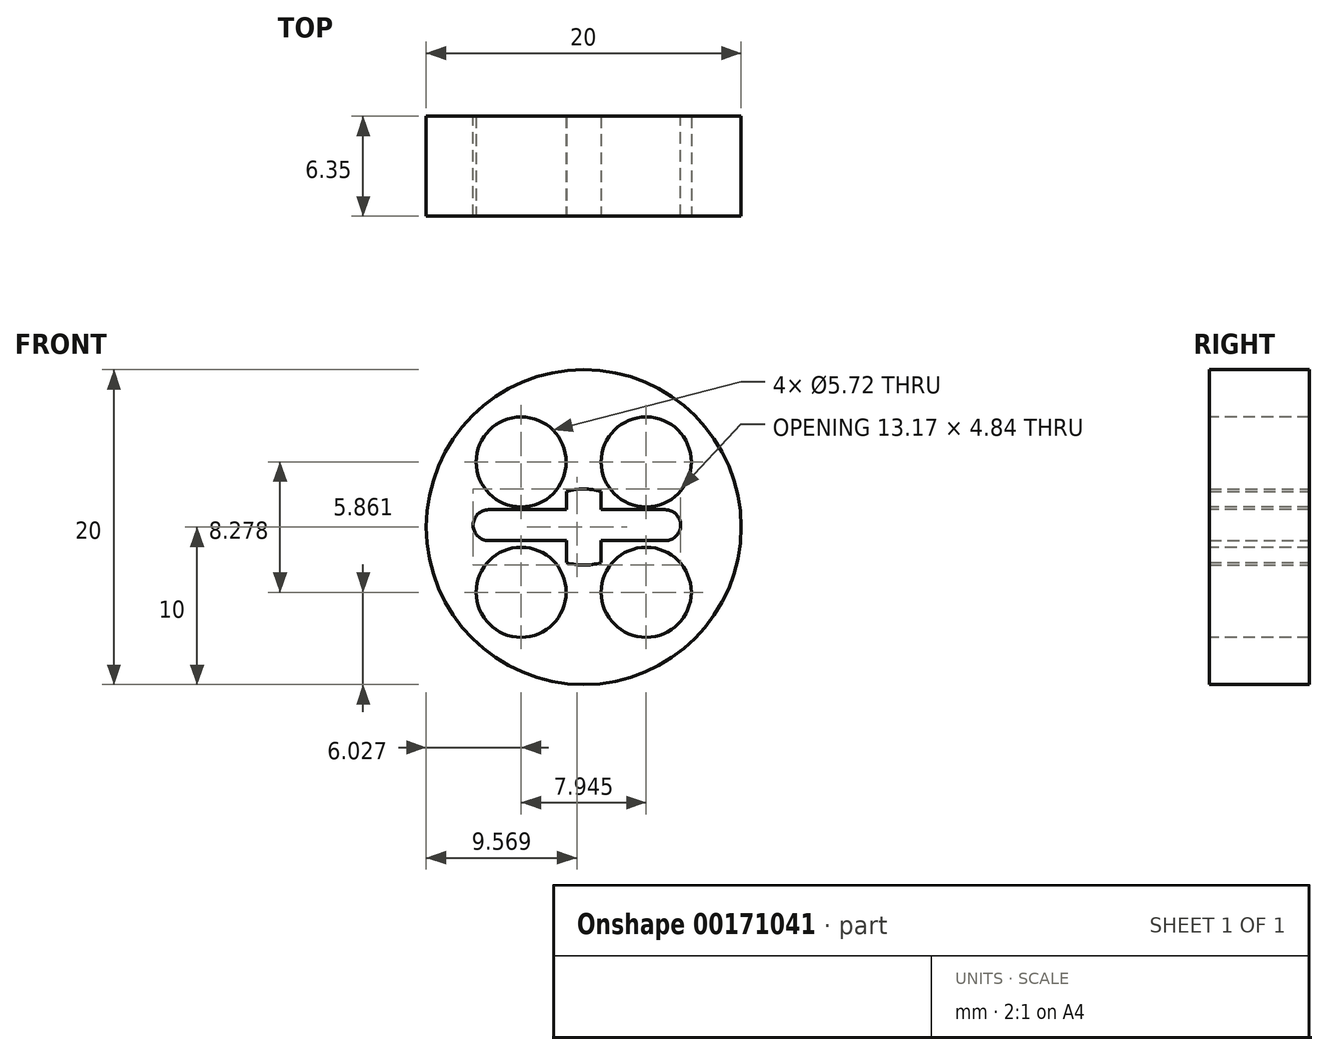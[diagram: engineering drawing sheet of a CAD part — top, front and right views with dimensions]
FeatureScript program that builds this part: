
annotation { "Feature Type Name" : "Feature", "Feature Type Description" : "" }
export const myFeature = defineFeature(function(context is Context, id is Id, definition is map)
    precondition{}
    {
        {
            var Q0;
            Q0=qCreatedBy(makeId("Front.planeOp"),FACE);
            var sketch = newSketch(context, id + "F0", { "sketchPlane" : qUnion([Q0])});
            skCircle(sketch, "E0", {"center": v(0, 0) * mm, "radius": 10 * mm});
            skSolve(sketch);
        }
        {
            var Q0;
            Q0 = qSketchRegion(id + "F0", true);
            extrude(context, id + "F1", {"entities" : qUnion([Q0]), "depth" : 6.35 * mm});
        }
        {
            var Q0;
            Q0=qCreatedBy(makeId("Front.planeOp"),FACE);
            var sketch = newSketch(context, id + "F2", { "sketchPlane" : qUnion([Q0])});
            skLineSegment(sketch, "E1", {"start": v(-6.04, 1.1) * mm, "end": v(5.17, 1.1) * mm});
            skLineSegment(sketch, "E2", {"start": v(5.17, -0.86) * mm, "end": v(-6.04, -0.86) * mm});
            skArc(sketch, "E3", {"start": v(-6.04, 1.1) * mm, "mid": v(-7.02, 0.12) * mm, "end": v(-6.04, -0.86) * mm});
            skArc(sketch, "E4", {"start": v(5.17, -0.86) * mm, "mid": v(6.16, 0.12) * mm, "end": v(5.17, 1.1) * mm});
            skSolve(sketch);
        }
        {
            var Q0;
            Q0 = qSketchRegion(id + "F2", true);
            extrude(context, id + "F3", {"entities" : qUnion([Q0]), "operationType" : NewBodyOperationType.REMOVE, "depth" : 25.4 * mm});
        }
        {
            var Q0;
            Q0=qCreatedBy(makeId("Front.planeOp"),FACE);
            var sketch = newSketch(context, id + "F4", { "sketchPlane" : qUnion([Q0])});
            skLineSegment(sketch, "E5", {"start": v(1.1, 0) * mm, "end": v(1.1, 2.26) * mm});
            skLineSegment(sketch, "E6", {"start": v(-1.1, 0) * mm, "end": v(-1.1, 2.26) * mm});
            skArc(sketch, "E7", {"start": v(1.1, 2.26) * mm, "mid": v(0, 2.42) * mm, "end": v(-1.1, 2.26) * mm});
            skLineSegment(sketch, "E8.MirrorCS", {"start": v(-1.1, 0) * mm, "end": v(-1.1, -2.26) * mm});
            skLineSegment(sketch, "E9.MirrorCS", {"start": v(1.1, 0) * mm, "end": v(1.1, -2.26) * mm});
            skArc(sketch, "E10.MirrorCS", {"start": v(1.1, -2.26) * mm, "mid": v(0, -2.42) * mm, "end": v(-1.1, -2.26) * mm});
            skSolve(sketch);
        }
        {
            var Q0;
            Q0 = qSketchRegion(id + "F4", true);
            extrude(context, id + "F5", {"entities" : qUnion([Q0]), "operationType" : NewBodyOperationType.REMOVE, "depth" : 25.4 * mm});
        }
        {
            var Q0;
            Q0=makeQuery(id+"F1.opExtrude","CAP_FACE",FACE,{"disambiguationData":[OSD([sQuery(id+"F0.wireOp",EDGE,"E0")])],"isStart":false});
            var sketch = newSketch(context, id + "F6", { "sketchPlane" : qUnion([Q0])});
            skCircle(sketch, "E11", {"center": v(-3.97, 4.14) * mm, "radius": 2.86 * mm});
            skPoint(sketch, "E12.centerSnap0", {"position": v(-3.57, -0.86) * mm});
            skLineSegment(sketch, "E13", {"start": v(0, 0) * mm, "end": v(-9.75, 0) * mm});
            skCircle(sketch, "E14.MirrorC", {"center": v(-3.97, -4.14) * mm, "radius": 2.86 * mm});
            skPoint(sketch, "E15.endSnap0", {"position": v(0, 2.42) * mm});
            skCircle(sketch, "E16.MirrorC", {"center": v(3.97, 4.14) * mm, "radius": 2.86 * mm});
            skCircle(sketch, "E17.MirrorC", {"center": v(3.97, -4.14) * mm, "radius": 2.86 * mm});
            skSolve(sketch);
        }
        {
            var Q0;
            Q0 = qSketchRegion(id + "F6", true);
            extrude(context, id + "F7", {"entities" : qUnion([Q0]), "operationType" : NewBodyOperationType.REMOVE, "oppositeDirection" : true, "depth" : 25.4 * mm});
        }
    });
